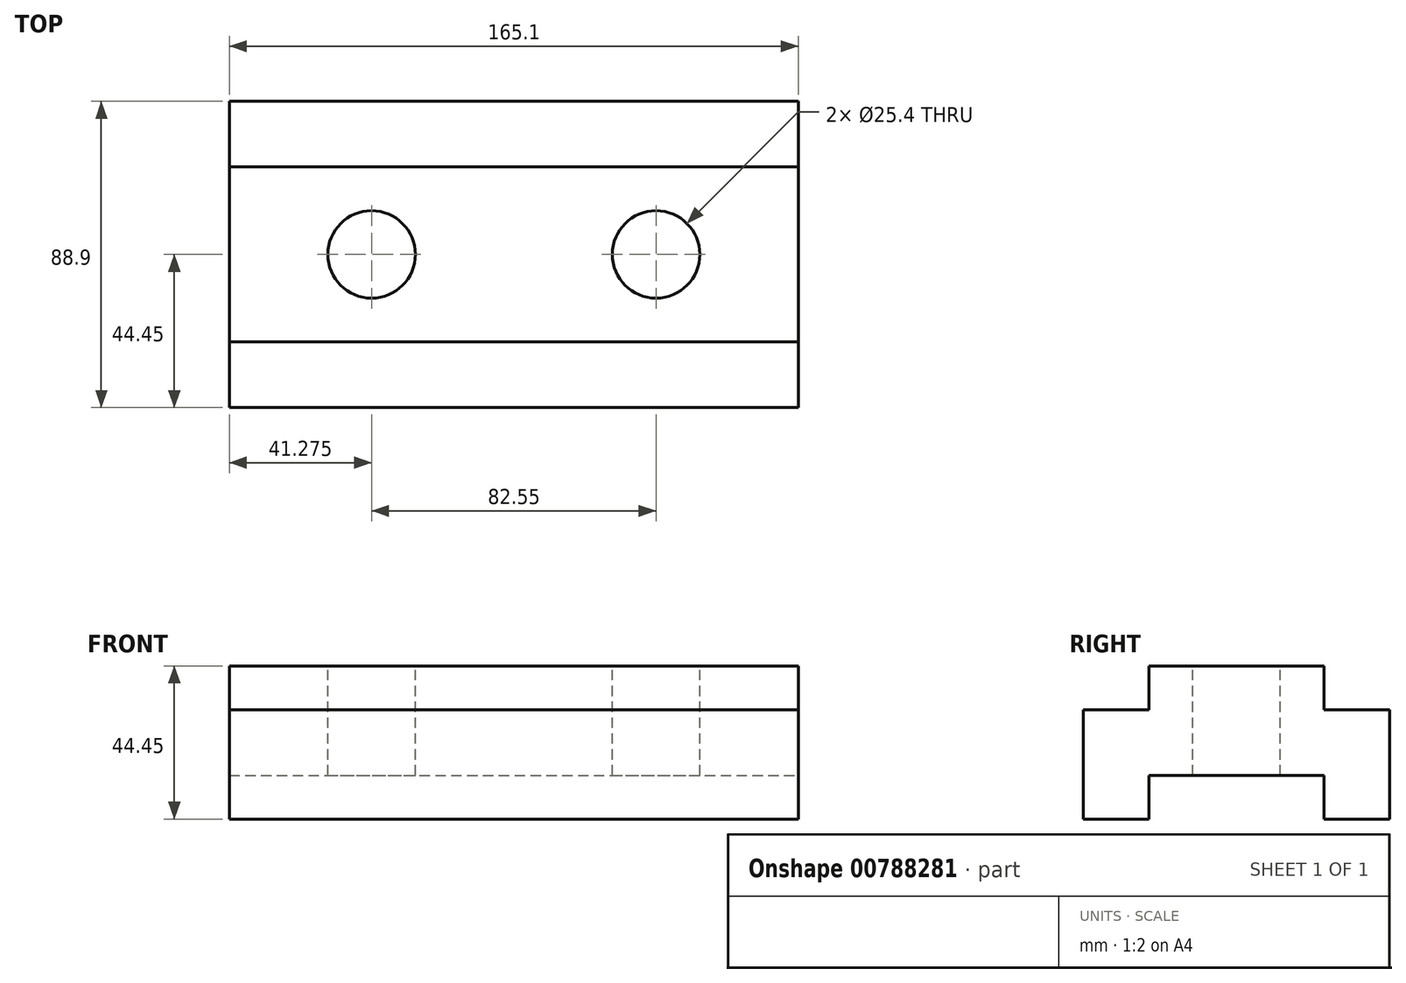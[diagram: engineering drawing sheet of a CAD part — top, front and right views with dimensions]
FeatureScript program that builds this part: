
annotation { "Feature Type Name" : "Feature", "Feature Type Description" : "" }
export const myFeature = defineFeature(function(context is Context, id is Id, definition is map)
    precondition{}
    {
        {
            var Q0;
            Q0=qCreatedBy(makeId("Front.planeOp"),FACE);
            var sketch = newSketch(context, id + "F0", { "sketchPlane" : qUnion([Q0])});
            skLineSegment(sketch, "E0", {"start": v(0, 0) * mm, "end": v(165.1, 0) * mm});
            skLineSegment(sketch, "E1", {"start": v(165.1, 0) * mm, "end": v(165.1, 44.45) * mm});
            skLineSegment(sketch, "E2", {"start": v(165.1, 44.45) * mm, "end": v(0, 44.45) * mm});
            skLineSegment(sketch, "E3", {"start": v(0, 44.45) * mm, "end": v(0, 0) * mm});
            skSolve(sketch);
        }
        {
            var Q0;
            Q0 = qSketchRegion(id + "F0", true);
            extrude(context, id + "F1", {"entities" : qUnion([Q0]), "depth" : 88.9 * mm, "offsetDistance" : 25.4 * mm});
        }
        {
            var Q0;
            Q0=makeQuery(id+"F1.opExtrude","SWEPT_FACE",FACE,{"disambiguationData":[OSD([sQuery(id+"F0.wireOp",EDGE,"E1")])]});
            var sketch = newSketch(context, id + "F2", { "sketchPlane" : qUnion([Q0])});
            skLineSegment(sketch, "E4", {"start": v(0, 44.45) * mm, "end": v(0, 31.75) * mm});
            skLineSegment(sketch, "E5", {"start": v(0, 31.75) * mm, "end": v(-19.05, 31.75) * mm});
            skLineSegment(sketch, "E6", {"start": v(-19.05, 31.75) * mm, "end": v(-19.05, 44.45) * mm});
            skLineSegment(sketch, "E7", {"start": v(-19.05, 44.45) * mm, "end": v(0, 44.45) * mm});
            skSolve(sketch);
        }
        {
            var Q0;
            Q0 = qSketchRegion(id + "F2", true);
            extrude(context, id + "F3", {"entities" : qUnion([Q0]), "operationType" : NewBodyOperationType.REMOVE, "oppositeDirection" : true, "depth" : 165.1 * mm, "offsetDistance" : 25.4 * mm});
        }
        {
            var Q0;
            Q0=makeQuery(id+"F1.opExtrude","SWEPT_FACE",FACE,{"disambiguationData":[OSD([sQuery(id+"F0.wireOp",EDGE,"E1")])]});
            var sketch = newSketch(context, id + "F4", { "sketchPlane" : qUnion([Q0])});
            skLineSegment(sketch, "E8", {"start": v(-88.9, 44.45) * mm, "end": v(-69.85, 44.45) * mm});
            skLineSegment(sketch, "E9", {"start": v(-69.85, 44.45) * mm, "end": v(-69.85, 31.75) * mm});
            skLineSegment(sketch, "E10", {"start": v(-69.85, 31.75) * mm, "end": v(-88.9, 31.75) * mm});
            skLineSegment(sketch, "E11", {"start": v(-88.9, 31.75) * mm, "end": v(-88.9, 44.45) * mm});
            skSolve(sketch);
        }
        {
            var Q0;
            Q0 = qSketchRegion(id + "F4", true);
            extrude(context, id + "F5", {"entities" : qUnion([Q0]), "operationType" : NewBodyOperationType.REMOVE, "oppositeDirection" : true, "depth" : 165.1 * mm, "offsetDistance" : 25.4 * mm});
        }
        {
            var Q0;
            Q0=makeQuery(id+"F1.opExtrude","SWEPT_FACE",FACE,{"disambiguationData":[OSD([sQuery(id+"F0.wireOp",EDGE,"E1")])]});
            var sketch = newSketch(context, id + "F6", { "sketchPlane" : qUnion([Q0])});
            skLineSegment(sketch, "E12", {"start": v(-69.85, 0) * mm, "end": v(-69.85, 12.7) * mm});
            skLineSegment(sketch, "E13", {"start": v(-69.85, 12.7) * mm, "end": v(-19.05, 12.7) * mm});
            skLineSegment(sketch, "E14", {"start": v(-19.05, 12.7) * mm, "end": v(-19.05, 0) * mm});
            skLineSegment(sketch, "E15", {"start": v(-19.05, 0) * mm, "end": v(-69.85, 0) * mm});
            skSolve(sketch);
        }
        {
            var Q0;
            Q0 = qSketchRegion(id + "F6", true);
            extrude(context, id + "F7", {"entities" : qUnion([Q0]), "operationType" : NewBodyOperationType.REMOVE, "oppositeDirection" : true, "depth" : 165.1 * mm, "offsetDistance" : 25.4 * mm});
        }
        {
            var Q0;
            Q0=makeQuery(id+"F1.opExtrude","SWEPT_FACE",FACE,{"disambiguationData":[OSD([sQuery(id+"F0.wireOp",EDGE,"E2")])]});
            var sketch = newSketch(context, id + "F8", { "sketchPlane" : qUnion([Q0])});
            skLineSegment(sketch, "E16", {"start": v(0, -69.85) * mm, "end": v(41.28, -69.85) * mm, "construction": true});
            skLineSegment(sketch, "E17", {"start": v(41.28, -69.85) * mm, "end": v(41.28, -44.45) * mm, "construction": true});
            skCircle(sketch, "E18", {"center": v(41.28, -44.45) * mm, "radius": 12.7 * mm});
            skSolve(sketch);
        }
        {
            var Q0;
            Q0 = qSketchRegion(id + "F8", true);
            extrude(context, id + "F9", {"entities" : qUnion([Q0]), "operationType" : NewBodyOperationType.REMOVE, "oppositeDirection" : true, "depth" : 38.1 * mm, "offsetDistance" : 25.4 * mm});
        }
        {
            var Q0;
            Q0=makeQuery(id+"F1.opExtrude","SWEPT_FACE",FACE,{"disambiguationData":[OSD([sQuery(id+"F0.wireOp",EDGE,"E2")])]});
            var sketch = newSketch(context, id + "F10", { "sketchPlane" : qUnion([Q0])});
            skLineSegment(sketch, "E19", {"start": v(165.1, -69.85) * mm, "end": v(123.83, -69.85) * mm, "construction": true});
            skLineSegment(sketch, "E20", {"start": v(123.83, -69.85) * mm, "end": v(123.83, -44.45) * mm, "construction": true});
            skCircle(sketch, "E21", {"center": v(123.83, -44.45) * mm, "radius": 12.7 * mm});
            skSolve(sketch);
        }
        {
            var Q0;
            Q0 = qSketchRegion(id + "F10", true);
            extrude(context, id + "F11", {"entities" : qUnion([Q0]), "operationType" : NewBodyOperationType.REMOVE, "oppositeDirection" : true, "depth" : 38.1 * mm, "offsetDistance" : 25.4 * mm});
        }
    });
